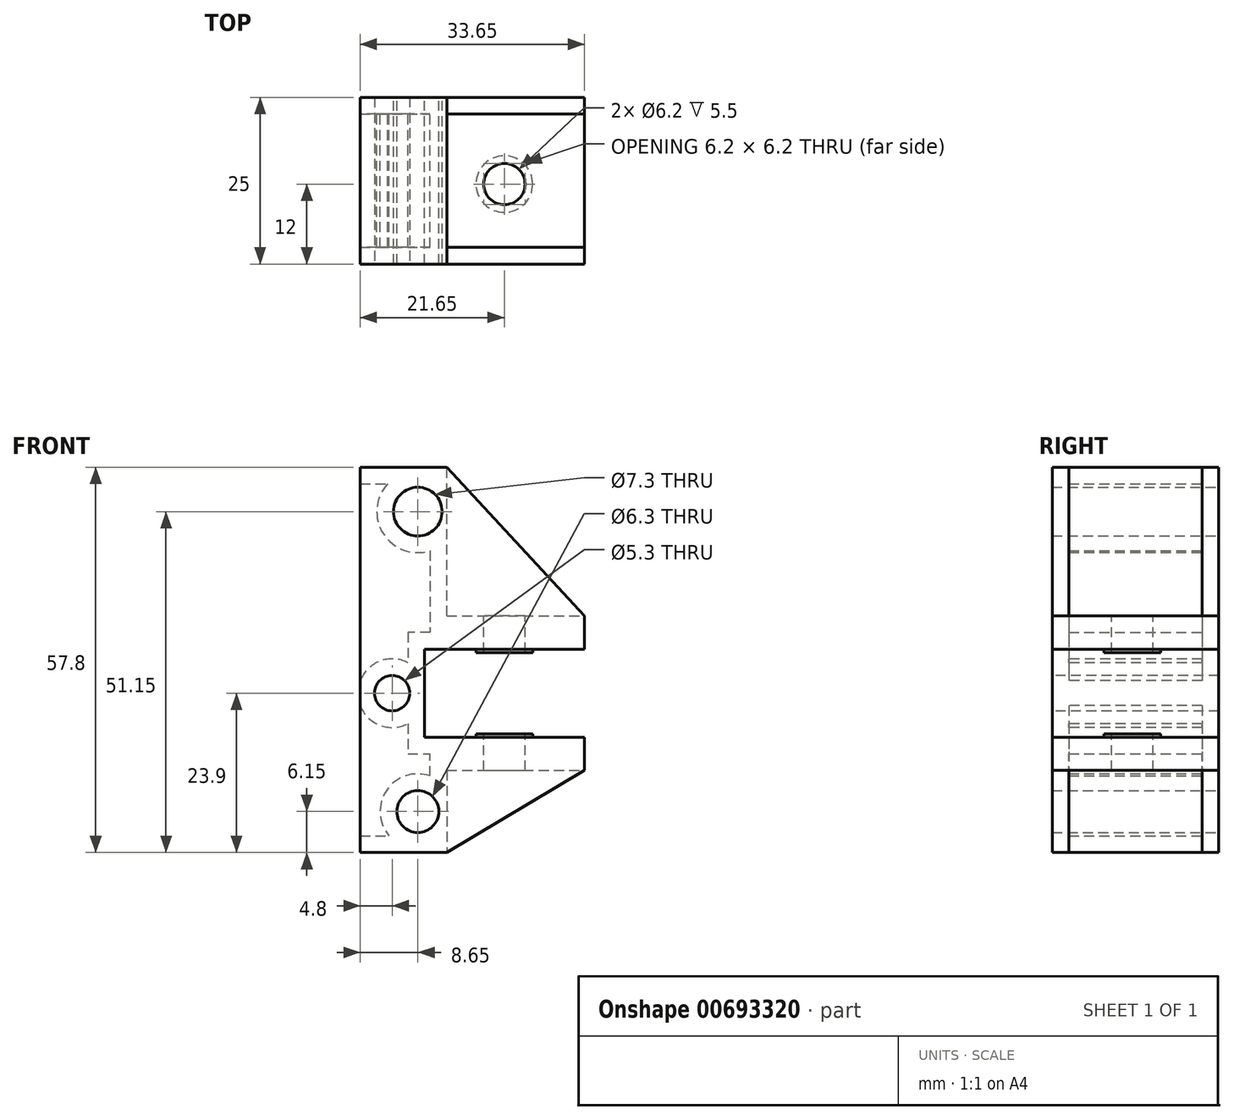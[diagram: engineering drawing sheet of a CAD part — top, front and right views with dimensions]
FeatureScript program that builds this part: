
annotation { "Feature Type Name" : "Feature", "Feature Type Description" : "" }
export const myFeature = defineFeature(function(context is Context, id is Id, definition is map)
    precondition{}
    {
        {
            var Q0;
            Q0=qCreatedBy(makeId("Front.planeOp"),FACE);
            var sketch = newSketch(context, id + "F0", { "sketchPlane" : qUnion([Q0])});
            skCircle(sketch, "E0", {"center": v(0, 22.5) * mm, "radius": 3.65 * mm});
            skCircle(sketch, "E1", {"center": v(0, -22.5) * mm, "radius": 3.15 * mm});
            skLineSegment(sketch, "E2.bottom", {"start": v(-8.65, 29.15) * mm, "end": v(4.35, 29.15) * mm});
            skLineSegment(sketch, "E2.top", {"start": v(-8.65, -28.65) * mm, "end": v(4.35, -28.65) * mm});
            skLineSegment(sketch, "E2.left", {"start": v(-8.65, 29.15) * mm, "end": v(-8.65, -28.65) * mm});
            skLineSegment(sketch, "E2.right", {"start": v(25, 6.85) * mm, "end": v(25, 1.85) * mm});
            skLineSegment(sketch, "E3", {"start": v(25, 1.85) * mm, "end": v(1, 1.85) * mm});
            skLineSegment(sketch, "E4", {"start": v(1, 1.85) * mm, "end": v(1, -11.35) * mm});
            skLineSegment(sketch, "E5", {"start": v(1, -11.35) * mm, "end": v(25, -11.35) * mm});
            skLineSegment(sketch, "E6", {"start": v(4.35, 29.15) * mm, "end": v(25, 6.85) * mm});
            skLineSegment(sketch, "E7", {"start": v(4.35, -28.65) * mm, "end": v(25, -16.35) * mm});
            skLineSegment(sketch, "E8.trimOffspring", {"start": v(25, -11.35) * mm, "end": v(25, -16.35) * mm});
            skSolve(sketch);
        }
        {
            var Q0;
            Q0=makeQuery(id+"F0.imprint","IMPRINT",FACE,{"disambiguationData":[TD([[makeQuery(id+"F0.imprint","IMPRINT",EDGE,{"derivedFrom":sQuery(id+"F0.wireOp",EDGE,"E0")}),-1.0]])]});
            extrude(context, id + "F1", {"entities" : qUnion([Q0]), "depth" : 25 * mm, "offsetDistance" : 25 * mm});
        }
        {
            var Q0;
            Q0=makeQuery(id+"F1.opExtrude","SWEPT_FACE",FACE,{"disambiguationData":[OSD([sQuery(id+"F0.wireOp",EDGE,"E5")])]});
            var sketch = newSketch(context, id + "F2", { "sketchPlane" : qUnion([Q0])});
            skCircle(sketch, "E9", {"center": v(13, -13) * mm, "radius": 3.1 * mm});
            skCircle(sketch, "E10", {"center": v(13, -13) * mm, "radius": 4.25 * mm});
            skSolve(sketch);
        }
        {
            var Q0;
            Q0=makeQuery(id+"F2.imprint","IMPRINT",FACE,{"disambiguationData":[TD([[makeQuery(id+"F2.imprint","IMPRINT",EDGE,{"derivedFrom":sQuery(id+"F2.wireOp",EDGE,"E9")}),1.0]])]});
            extrude(context, id + "F3", {"entities" : qUnion([Q0]), "operationType" : NewBodyOperationType.REMOVE, "endBound" : BoundingType.THROUGH_ALL, "oppositeDirection" : true, "depth" : 25 * mm, "offsetDistance" : 25 * mm, "hasSecondDirection" : true, "secondDirectionBound" : SecondDirectionBoundingType.THROUGH_ALL, "secondDirectionOppositeDirection" : false, "secondDirectionDepth" : 25 * mm});
        }
        {
            var Q0;
            Q0=makeQuery(id+"F2.imprint","IMPRINT",FACE,{"disambiguationData":[TD([[makeQuery(id+"F2.imprint","IMPRINT",EDGE,{"derivedFrom":sQuery(id+"F2.wireOp",EDGE,"E9")}),-1.0]])]});
            extrude(context, id + "F4", {"entities" : qUnion([Q0]), "operationType" : NewBodyOperationType.ADD, "depth" : 0.5 * mm, "offsetDistance" : 25 * mm});
        }
        {
            var Q0;
            Q0=makeQuery(id+"F1.opExtrude","SWEPT_FACE",FACE,{"disambiguationData":[OSD([sQuery(id+"F0.wireOp",EDGE,"E3")])]});
            var sketch = newSketch(context, id + "F5", { "sketchPlane" : qUnion([Q0])});
            skCircle(sketch, "E11", {"center": v(13, 13) * mm, "radius": 4.25 * mm});
            skCircle(sketch, "E12", {"center": v(13, 13) * mm, "radius": 3.1 * mm});
            skLineSegment(sketch, "E13.bottom", {"start": v(1, 22.5) * mm, "end": v(25, 22.5) * mm});
            skLineSegment(sketch, "E13.top", {"start": v(1, 2.5) * mm, "end": v(25, 2.5) * mm});
            skLineSegment(sketch, "E13.left", {"start": v(1, 22.5) * mm, "end": v(1, 2.5) * mm});
            skLineSegment(sketch, "E13.right", {"start": v(25, 22.5) * mm, "end": v(25, 2.5) * mm});
            skSolve(sketch);
        }
        {
            var Q0;
            Q0=makeQuery(id+"F5.imprint","IMPRINT",FACE,{"disambiguationData":[TD([[makeQuery(id+"F5.imprint","IMPRINT",EDGE,{"derivedFrom":sQuery(id+"F5.wireOp",EDGE,"E11")}),1.0]])]});
            extrude(context, id + "F6", {"entities" : qUnion([Q0]), "operationType" : NewBodyOperationType.ADD, "depth" : 0.5 * mm, "offsetDistance" : 25 * mm});
        }
        {
            var Q0;
            Q0=makeQuery(id+"F1.opExtrude","SWEPT_FACE",FACE,{"disambiguationData":[OSD([sQuery(id+"F0.wireOp",EDGE,"E2.bottom")])]});
            var sketch = newSketch(context, id + "F7", { "sketchPlane" : qUnion([Q0])});
            skLineSegment(sketch, "E14.bottom", {"start": v(4.35, -22.5) * mm, "end": v(25, -22.5) * mm});
            skLineSegment(sketch, "E14.top", {"start": v(4.35, -2.5) * mm, "end": v(25, -2.5) * mm});
            skLineSegment(sketch, "E14.left", {"start": v(4.35, -22.5) * mm, "end": v(4.35, -2.5) * mm});
            skLineSegment(sketch, "E14.right", {"start": v(25, -22.5) * mm, "end": v(25, -2.5) * mm});
            skSolve(sketch);
        }
        {
            var Q0;
            Q0=makeQuery(id+"F7.imprint","IMPRINT",FACE,{"disambiguationData":[TD([[makeQuery(id+"F7.imprint","IMPRINT",EDGE,{"derivedFrom":sQuery(id+"F7.wireOp",EDGE,"E14.bottom")}),1.0]])]});
            extrude(context, id + "F8", {"entities" : qUnion([Q0]), "operationType" : NewBodyOperationType.REMOVE, "oppositeDirection" : true, "depth" : 22.3 * mm, "offsetDistance" : 25 * mm});
        }
        {
            var Q0;
            Q0=makeQuery(id+"F1.opExtrude","SWEPT_FACE",FACE,{"disambiguationData":[OSD([sQuery(id+"F0.wireOp",EDGE,"E2.top")])]});
            var sketch = newSketch(context, id + "F9", { "sketchPlane" : qUnion([Q0])});
            skLineSegment(sketch, "E15.bottom", {"start": v(4.35, 22.5) * mm, "end": v(25, 22.5) * mm});
            skLineSegment(sketch, "E15.top", {"start": v(4.35, 2.5) * mm, "end": v(25, 2.5) * mm});
            skLineSegment(sketch, "E15.left", {"start": v(4.35, 22.5) * mm, "end": v(4.35, 2.5) * mm});
            skLineSegment(sketch, "E15.right", {"start": v(25, 22.5) * mm, "end": v(25, 2.5) * mm});
            skSolve(sketch);
        }
        {
            var Q0;
            Q0 = qSketchRegion(id + "F9", true);
            extrude(context, id + "F10", {"entities" : qUnion([Q0]), "operationType" : NewBodyOperationType.REMOVE, "oppositeDirection" : true, "depth" : 12.3 * mm, "offsetDistance" : 25 * mm});
        }
        {
            var Q0;
            Q0=makeQuery(id+"F1.opExtrude","CAP_FACE",FACE,{"disambiguationData":[OSD([sQuery(id+"F0.wireOp",EDGE,"E0"),sQuery(id+"F0.wireOp",EDGE,"E1"),sQuery(id+"F0.wireOp",EDGE,"E2.bottom"),sQuery(id+"F0.wireOp",EDGE,"E2.top"),sQuery(id+"F0.wireOp",EDGE,"E2.left"),sQuery(id+"F0.wireOp",EDGE,"E2.right"),sQuery(id+"F0.wireOp",EDGE,"E3"),sQuery(id+"F0.wireOp",EDGE,"E4"),sQuery(id+"F0.wireOp",EDGE,"E5"),sQuery(id+"F0.wireOp",EDGE,"E6"),sQuery(id+"F0.wireOp",EDGE,"E7"),sQuery(id+"F0.wireOp",EDGE,"E8.trimOffspring")])],"isStart":false});
            var sketch = newSketch(context, id + "F11", { "sketchPlane" : qUnion([Q0])});
            skCircle(sketch, "E16", {"center": v(-3.85, -4.75) * mm, "radius": 2.65 * mm});
            skSolve(sketch);
        }
        {
            var Q0;
            Q0=makeQuery(id+"F11.imprint","IMPRINT",FACE,{"disambiguationData":[TD([[makeQuery(id+"F11.imprint","IMPRINT",EDGE,{"derivedFrom":sQuery(id+"F11.wireOp",EDGE,"E16")}),1.0]])]});
            extrude(context, id + "F12", {"entities" : qUnion([Q0]), "operationType" : NewBodyOperationType.REMOVE, "endBound" : BoundingType.THROUGH_ALL, "oppositeDirection" : true, "depth" : 25 * mm, "offsetDistance" : 25 * mm});
        }
        {
            var Q0;
            Q0=makeQuery(id+"F1.opExtrude","SWEPT_FACE",FACE,{"disambiguationData":[OSD([sQuery(id+"F0.wireOp",EDGE,"E2.left")])]});
            shell(context, id + "F13", {"entities" : qUnion([Q0]), "thickness" : 2.5 * mm});
        }
    });
